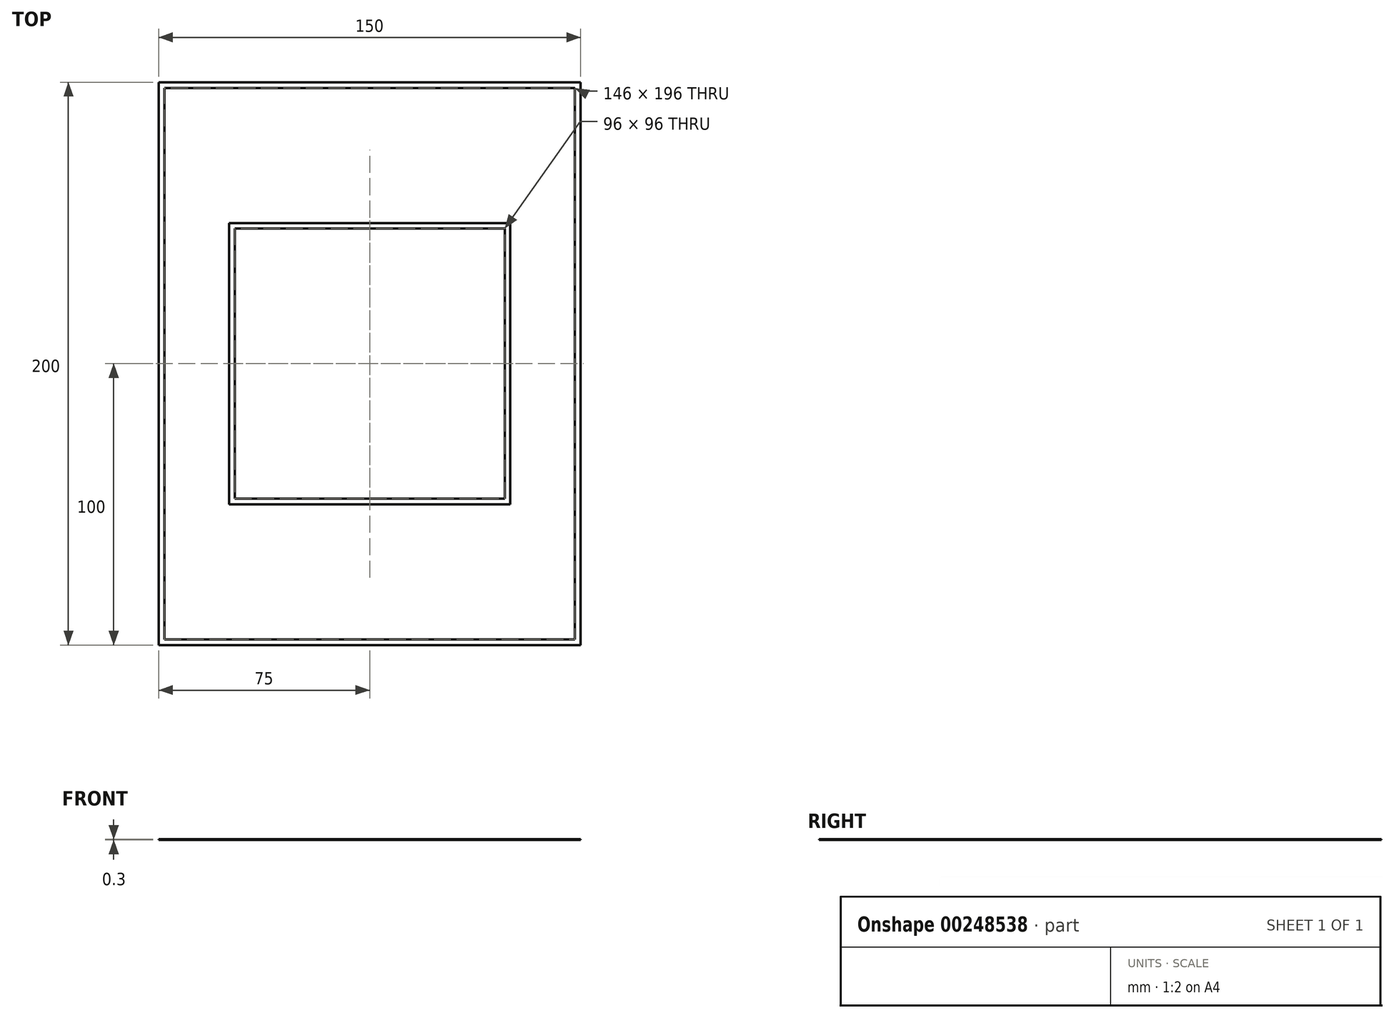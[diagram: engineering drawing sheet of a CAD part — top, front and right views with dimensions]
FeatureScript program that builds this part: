
annotation { "Feature Type Name" : "Feature", "Feature Type Description" : "" }
export const myFeature = defineFeature(function(context is Context, id is Id, definition is map)
    precondition{}
    {
        {
            var Q0;
            Q0=qCreatedBy(makeId("Top.planeOp"),FACE);
            var sketch = newSketch(context, id + "F0", { "sketchPlane" : qUnion([Q0])});
            skLineSegment(sketch, "E0.bottom", {"start": v(-75, 100) * mm, "end": v(75, 100) * mm});
            skLineSegment(sketch, "E0.top", {"start": v(-75, -100) * mm, "end": v(75, -100) * mm});
            skLineSegment(sketch, "E0.left", {"start": v(-75, 100) * mm, "end": v(-75, -100) * mm});
            skLineSegment(sketch, "E0.right", {"start": v(75, 100) * mm, "end": v(75, -100) * mm});
            skLineSegment(sketch, "E1.bottom", {"start": v(-73, 98) * mm, "end": v(73, 98) * mm});
            skLineSegment(sketch, "E1.top", {"start": v(-73, -98) * mm, "end": v(73, -98) * mm});
            skLineSegment(sketch, "E1.left", {"start": v(-73, 98) * mm, "end": v(-73, -98) * mm});
            skLineSegment(sketch, "E1.right", {"start": v(73, 98) * mm, "end": v(73, -98) * mm});
            skLineSegment(sketch, "E2.bottom", {"start": v(-50, 50) * mm, "end": v(50, 50) * mm});
            skLineSegment(sketch, "E2.top", {"start": v(-50, -50) * mm, "end": v(50, -50) * mm});
            skLineSegment(sketch, "E2.left", {"start": v(-50, 50) * mm, "end": v(-50, -50) * mm});
            skLineSegment(sketch, "E2.right", {"start": v(50, 50) * mm, "end": v(50, -50) * mm});
            skLineSegment(sketch, "E3.bottom", {"start": v(-48, 48) * mm, "end": v(48, 48) * mm});
            skLineSegment(sketch, "E3.top", {"start": v(-48, -48) * mm, "end": v(48, -48) * mm});
            skLineSegment(sketch, "E3.left", {"start": v(-48, 48) * mm, "end": v(-48, -48) * mm});
            skLineSegment(sketch, "E3.right", {"start": v(48, 48) * mm, "end": v(48, -48) * mm});
            skSolve(sketch);
        }
        {
            var Q0;
            Q0=makeQuery(id+"F0.imprint","IMPRINT",FACE,{"disambiguationData":[TD([[makeQuery(id+"F0.imprint","IMPRINT",EDGE,{"derivedFrom":sQuery(id+"F0.wireOp",EDGE,"E2.bottom")}),-1.0]])]});
            var Q1;
            Q1=makeQuery(id+"F0.imprint","IMPRINT",FACE,{"disambiguationData":[TD([[makeQuery(id+"F0.imprint","IMPRINT",EDGE,{"derivedFrom":sQuery(id+"F0.wireOp",EDGE,"E0.bottom")}),-1.0]])]});
            extrude(context, id + "F1", {"entities" : qUnion([Q0, Q1]), "depth" : .3 * mm});
        }
    });
